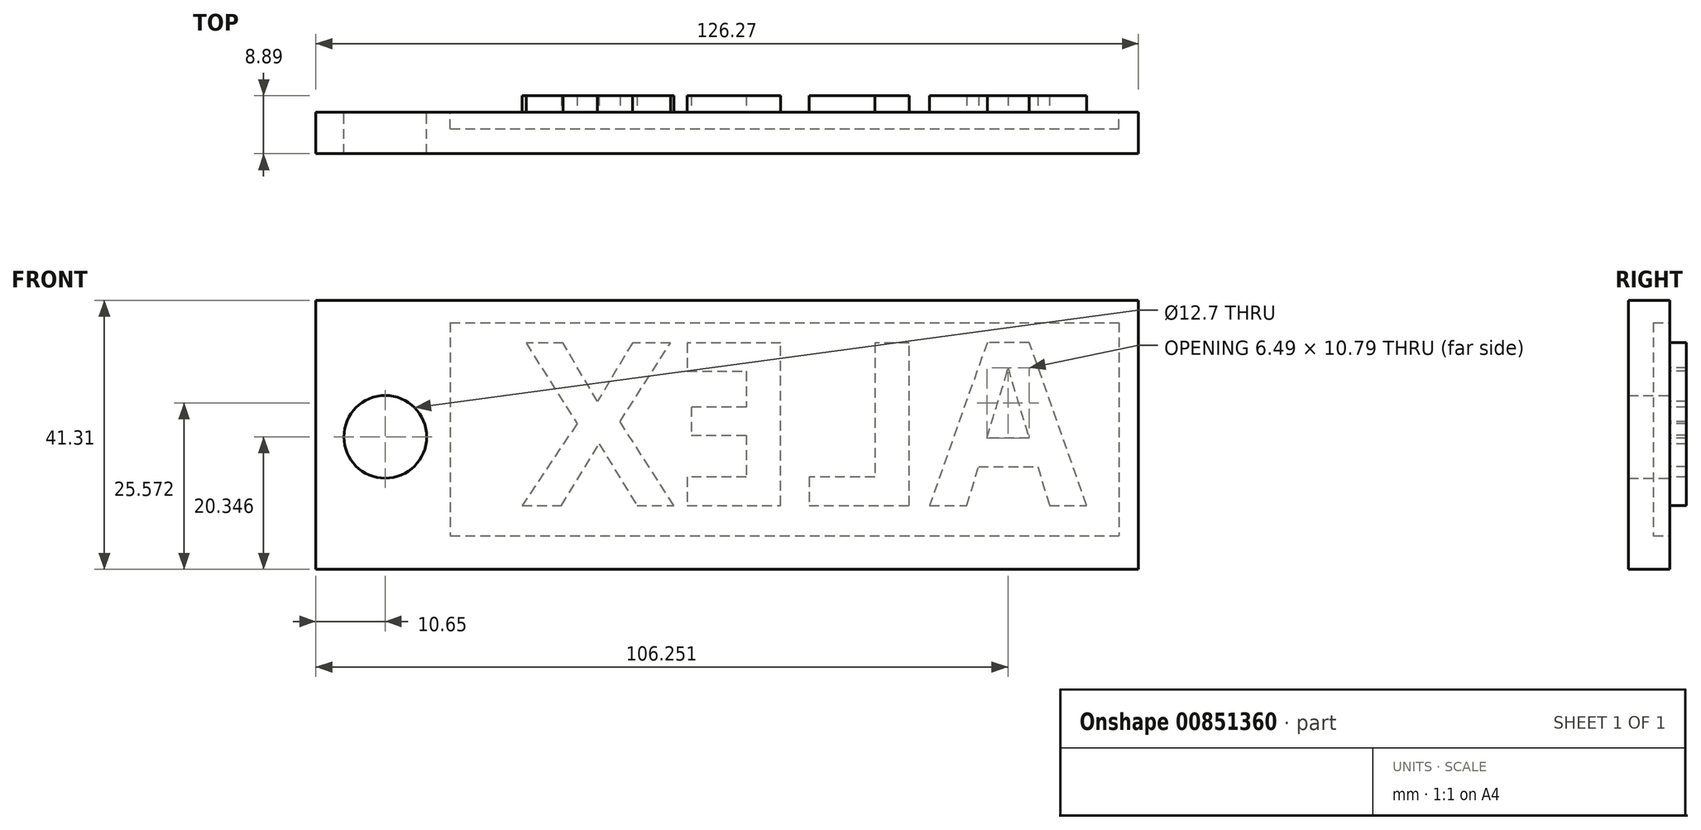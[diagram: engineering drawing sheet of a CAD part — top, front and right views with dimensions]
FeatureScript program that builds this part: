
annotation { "Feature Type Name" : "Feature", "Feature Type Description" : "" }
export const myFeature = defineFeature(function(context is Context, id is Id, definition is map)
    precondition{}
    {
        {
            var Q0;
            Q0=qCreatedBy(makeId("Front.planeOp"),FACE);
            var sketch = newSketch(context, id + "F0", { "sketchPlane" : qUnion([Q0])});
            skLineSegment(sketch, "E0.bottom", {"start": v(-76.06, 38.35) * mm, "end": v(50.21, 38.35) * mm});
            skLineSegment(sketch, "E0.top", {"start": v(-76.06, -2.96) * mm, "end": v(50.21, -2.96) * mm});
            skLineSegment(sketch, "E0.left", {"start": v(-76.06, 38.35) * mm, "end": v(-76.06, -2.96) * mm});
            skLineSegment(sketch, "E0.right", {"start": v(50.21, 38.35) * mm, "end": v(50.21, -2.96) * mm});
            skSolve(sketch);
        }
        {
            var Q0;
            Q0=makeQuery(id+"F0.imprint","IMPRINT",FACE,{"disambiguationData":[TD([[makeQuery(id+"F0.imprint","IMPRINT",EDGE,{"derivedFrom":sQuery(id+"F0.wireOp",EDGE,"E0.bottom")}),-1.0]])]});
            extrude(context, id + "F1", {"entities" : qUnion([Q0]), "depth" : 6.35 * mm, "offsetDistance" : 25.4 * mm});
        }
        {
            var Q0;
            Q0=qCreatedBy(makeId("Front.planeOp"),FACE);
            var sketch = newSketch(context, id + "F2", { "sketchPlane" : qUnion([Q0])});
            skLineSegment(sketch, "E1.bottom", {"start": v(-55.42, 34.93) * mm, "end": v(47.22, 34.93) * mm});
            skLineSegment(sketch, "E1.top", {"start": v(-55.42, 2.22) * mm, "end": v(47.22, 2.22) * mm});
            skLineSegment(sketch, "E1.left", {"start": v(-55.42, 34.93) * mm, "end": v(-55.42, 2.22) * mm});
            skLineSegment(sketch, "E1.right", {"start": v(47.22, 34.93) * mm, "end": v(47.22, 2.22) * mm});
            skSolve(sketch);
        }
        {
            var Q0;
            Q0=makeQuery(id+"F2.imprint","IMPRINT",FACE,{"disambiguationData":[TD([[makeQuery(id+"F2.imprint","IMPRINT",EDGE,{"derivedFrom":sQuery(id+"F2.wireOp",EDGE,"E1.bottom")}),-1.0]])]});
            extrude(context, id + "F3", {"entities" : qUnion([Q0]), "operationType" : NewBodyOperationType.REMOVE, "depth" : 2.54 * mm, "offsetDistance" : 25.4 * mm});
        }
        {
            var Q0;
            Q0=makeQuery(id+"F1.opExtrude","CAP_FACE",FACE,{"disambiguationData":[OSD([sQuery(id+"F0.wireOp",EDGE,"E0.bottom"),sQuery(id+"F0.wireOp",EDGE,"E0.top"),sQuery(id+"F0.wireOp",EDGE,"E0.left"),sQuery(id+"F0.wireOp",EDGE,"E0.right")])],"isStart":true});
            var sketch = newSketch(context, id + "F4", { "sketchPlane" : qUnion([Q0])});
            skText(sketch, "E2", { "text": "ALEX\n", "fontName": "OpenSans-Bold.ttf"});
            const initialGuessF4  = {"E2": [-0.04227, 0.00685, 1, 0, 0.02514]};
            skSetInitialGuess(sketch, initialGuessF4);
            skSolve(sketch);
        }
        {
            var Q0;
            Q0=makeQuery(id+"F4.imprint","IMPRINT",FACE,{"disambiguationData":[TD([[makeQuery(id+"F4.imprint","IMPRINT",EDGE,{"derivedFrom":sQuery(id+"F4.wireOp",EDGE,"E2.sketch_text.stroke-30")}),-1.0]])]});
            extrude(context, id + "F5", {"entities" : qUnion([Q0]), "depth" : 2.54 * mm, "offsetDistance" : 25.4 * mm});
        }
        {
            var Q0;
            Q0 = qSketchRegion(id + "F4", true);
            extrude(context, id + "F6", {"entities" : qUnion([Q0]), "operationType" : NewBodyOperationType.ADD, "depth" : 2.54 * mm, "offsetDistance" : 25.4 * mm});
        }
        {
            var Q0;
            Q0=makeQuery(id+"F0.imprint","IMPRINT",FACE,{"disambiguationData":[TD([[makeQuery(id+"F0.imprint","IMPRINT",EDGE,{"derivedFrom":sQuery(id+"F0.wireOp",EDGE,"E0.bottom")}),-1.0]])]});
            var sketch = newSketch(context, id + "F7", { "sketchPlane" : qUnion([Q0])});
            skPoint(sketch, "E3", {"position": v(-65.41, 17.39) * mm});
            skSolve(sketch);
        }
        {
            var Q0;
            Q0=sQuery(id+"F7.wireOp",VERTEX,"E3");
            var Q1;
            Q1=makeQuery(id+"F1.opExtrude","SWEPT_BODY",BODY,{"disambiguationData":[OSD([sQuery(id+"F0.wireOp",EDGE,"E0.bottom"),sQuery(id+"F0.wireOp",EDGE,"E0.top"),sQuery(id+"F0.wireOp",EDGE,"E0.left"),sQuery(id+"F0.wireOp",EDGE,"E0.right")])]});
            hole(context, id + "F8", {"style" : HoleStyle.C_BORE, "endStyle" : HoleEndStyle.THROUGH, "oppositeDirection" : true, "holeDiameter" : 6.35 * mm, "cBoreDiameter" : 12.7 * mm, "cBoreDepth" : 6.35 * mm, "majorDiameter" : 6.35 * mm, "isTappedThrough" : true, "tappedDepth" : 12.7 * mm, "tapClearance" : 3, "locations" : qUnion([Q0]), "scope" : qUnion([Q1])});
        }
    });
